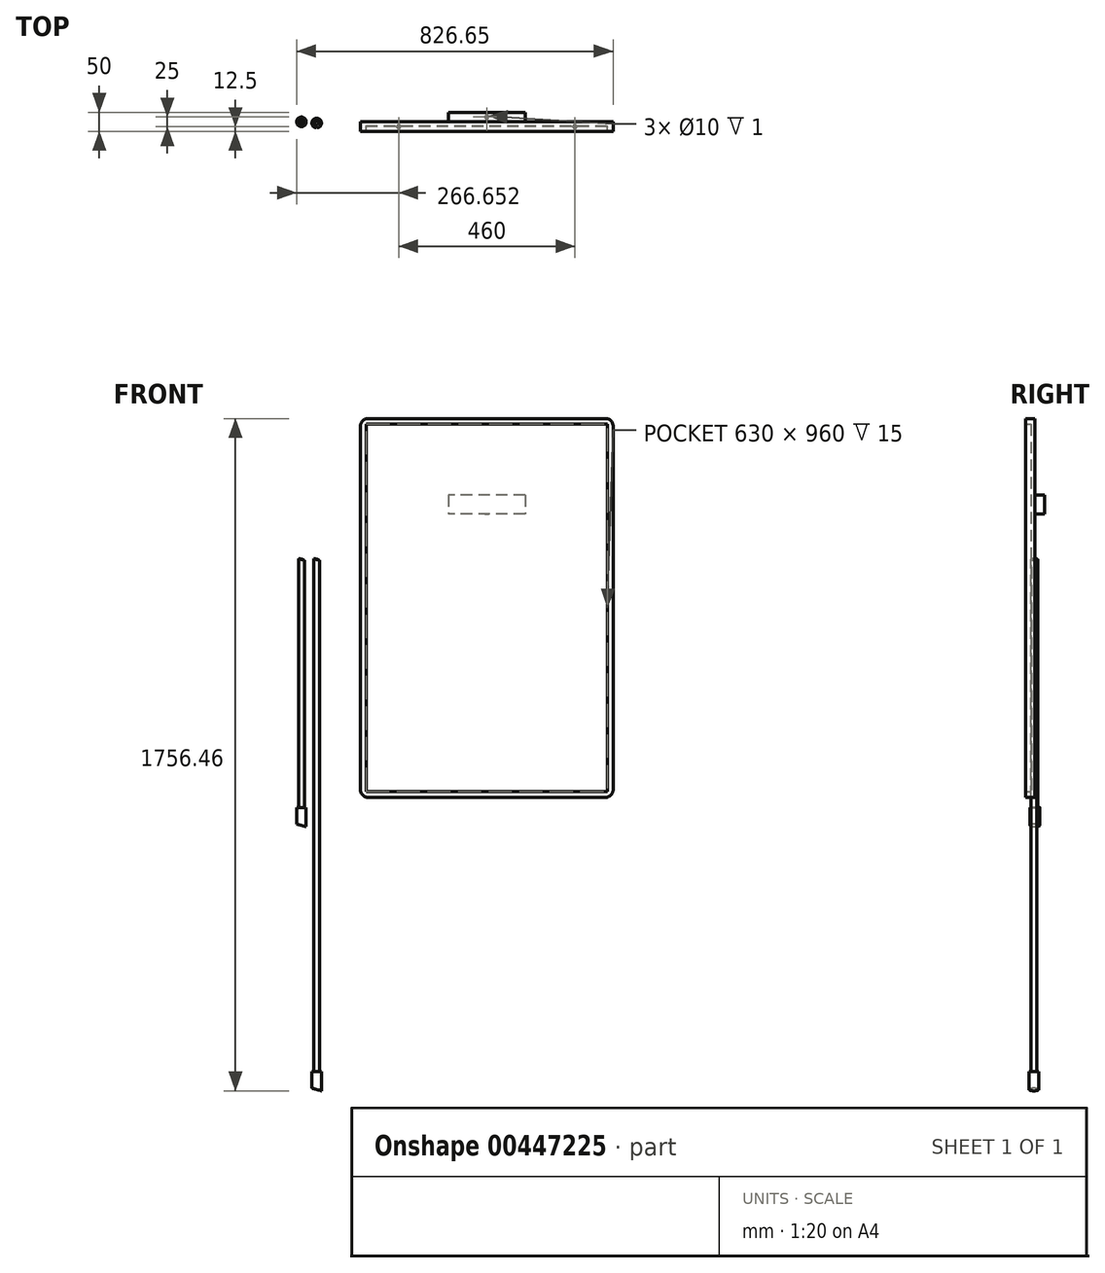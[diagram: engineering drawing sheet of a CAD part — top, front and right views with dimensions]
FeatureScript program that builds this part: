
annotation { "Feature Type Name" : "Feature", "Feature Type Description" : "" }
export const myFeature = defineFeature(function(context is Context, id is Id, definition is map)
    precondition{}
    {
        {
            var Q0;
            Q0=qCreatedBy(makeId("Top.planeOp"),FACE);
            var sketch = newSketch(context, id + "F0", { "sketchPlane" : qUnion([Q0])});
            skCircle(sketch, "E0", {"center": v(0, 0) * mm, "radius": 7.5 * mm});
            skCircle(sketch, "E1", {"center": v(39.86, -2.97) * mm, "radius": 7.5 * mm});
            skSolve(sketch);
        }
        {
            var Q0;
            Q0=makeQuery(id+"F0.imprint","IMPRINT",FACE,{"disambiguationData":[TD([[makeQuery(id+"F0.imprint","IMPRINT",EDGE,{"derivedFrom":sQuery(id+"F0.wireOp",EDGE,"E0")}),1.0]])]});
            extrude(context, id + "F1", {"entities" : qUnion([Q0]), "oppositeDirection" : true, "depth" : 700 * mm});
        }
        {
            var Q0;
            Q0=makeQuery(id+"F0.imprint","IMPRINT",FACE,{"disambiguationData":[TD([[makeQuery(id+"F0.imprint","IMPRINT",EDGE,{"derivedFrom":sQuery(id+"F0.wireOp",EDGE,"E1")}),1.0]])]});
            extrude(context, id + "F2", {"entities" : qUnion([Q0]), "oppositeDirection" : true, "depth" : 1390 * mm});
        }
        {
            var Q0;
            Q0=makeQuery(id+"F2.opExtrude","CAP_FACE",FACE,{"disambiguationData":[OSD([sQuery(id+"F0.wireOp",EDGE,"E1")])],"isStart":false});
            var sketch = newSketch(context, id + "F3", { "sketchPlane" : qUnion([Q0])});
            skCircle(sketch, "E2", {"center": v(39.86, 2.97) * mm, "radius": 12.5 * mm});
            skSolve(sketch);
        }
        {
            var Q0;
            Q0=makeQuery(id+"F3.imprint","IMPRINT",FACE,{"disambiguationData":[TD([[makeQuery(id+"F3.imprint","IMPRINT",EDGE,{"derivedFrom":sQuery(id+"F3.wireOp",EDGE,"E2")}),1.0]])]});
            extrude(context, id + "F4", {"entities" : qUnion([Q0]), "operationType" : NewBodyOperationType.ADD, "oppositeDirection" : true, "depth" : 50 * mm});
        }
        {
            var Q0;
            Q0=makeQuery(id+"F1.opExtrude","CAP_FACE",FACE,{"disambiguationData":[OSD([sQuery(id+"F0.wireOp",EDGE,"E0")])],"isStart":false});
            var sketch = newSketch(context, id + "F5", { "sketchPlane" : qUnion([Q0])});
            skCircle(sketch, "E3", {"center": v(0, 0) * mm, "radius": 12.5 * mm});
            skSolve(sketch);
        }
        {
            var Q0;
            Q0=makeQuery(id+"F5.imprint","IMPRINT",FACE,{"disambiguationData":[TD([[makeQuery(id+"F5.imprint","IMPRINT",EDGE,{"derivedFrom":sQuery(id+"F5.wireOp",EDGE,"E3")}),1.0]])]});
            extrude(context, id + "F6", {"entities" : qUnion([Q0]), "operationType" : NewBodyOperationType.ADD, "oppositeDirection" : true, "depth" : 50 * mm});
        }
        {
            var Q0;
            Q0=qCreatedBy(makeId("Front.planeOp"),FACE);
            var sketch = newSketch(context, id + "F7", { "sketchPlane" : qUnion([Q0])});
            skLineSegment(sketch, "E4", {"start": v(7.5, 0) * mm, "end": v(-7.5, 0) * mm});
            skLineSegment(sketch, "E5", {"start": v(-7.5, 0) * mm, "end": v(7.5, -4.02) * mm});
            skLineSegment(sketch, "E6", {"start": v(7.5, -4.02) * mm, "end": v(7.5, 0) * mm});
            skLineSegment(sketch, "E7", {"start": v(47.36, 0) * mm, "end": v(32.36, 0) * mm});
            skLineSegment(sketch, "E8", {"start": v(32.36, 0) * mm, "end": v(47.36, -4.02) * mm});
            skLineSegment(sketch, "E9", {"start": v(47.36, -4.02) * mm, "end": v(47.36, 0) * mm});
            skLineSegment(sketch, "E10", {"start": v(12.5, -700) * mm, "end": v(-12.5, -700) * mm});
            skLineSegment(sketch, "E11", {"start": v(52.36, -1390) * mm, "end": v(27.36, -1390) * mm});
            skPoint(sketch, "E12", {"position": v(0, -700) * mm});
            skPoint(sketch, "E13", {"position": v(39.86, -1390) * mm});
            skLineSegment(sketch, "E14", {"start": v(12.5, -700) * mm, "end": v(-12.5, -693.3) * mm});
            skLineSegment(sketch, "E15", {"start": v(-12.5, -693.3) * mm, "end": v(-12.5, -700) * mm});
            skLineSegment(sketch, "E16", {"start": v(52.36, -1390) * mm, "end": v(27.36, -1383.3) * mm});
            skLineSegment(sketch, "E17", {"start": v(27.36, -1383.3) * mm, "end": v(27.36, -1390) * mm});
            skSolve(sketch);
        }
        {
            var Q0;
            Q0 = qSketchRegion(id + "F7", true);
            extrude(context, id + "F8", {"entities" : qUnion([Q0]), "operationType" : NewBodyOperationType.REMOVE, "endBound" : BoundingType.THROUGH_ALL, "oppositeDirection" : true, "depth" : 25 * mm, "hasSecondDirection" : true, "secondDirectionBound" : SecondDirectionBoundingType.THROUGH_ALL, "secondDirectionOppositeDirection" : false, "secondDirectionDepth" : 25 * mm});
        }
        {
            var Q0;
            Q0=qCreatedBy(makeId("Front.planeOp"),FACE);
            var sketch = newSketch(context, id + "F9", { "sketchPlane" : qUnion([Q0])});
            skLineSegment(sketch, "E18.bottom", {"start": v(169.15, 351.46) * mm, "end": v(799.15, 351.46) * mm});
            skLineSegment(sketch, "E18.top", {"start": v(169.15, -608.54) * mm, "end": v(799.15, -608.54) * mm});
            skLineSegment(sketch, "E18.left", {"start": v(169.15, 351.46) * mm, "end": v(169.15, -608.54) * mm});
            skLineSegment(sketch, "E18.right", {"start": v(799.15, 351.46) * mm, "end": v(799.15, -608.54) * mm});
            skSolve(sketch);
        }
        {
            var Q0;
            Q0=makeQuery(id+"F9.imprint","IMPRINT",FACE,{"disambiguationData":[TD([[makeQuery(id+"F9.imprint","IMPRINT",EDGE,{"derivedFrom":sQuery(id+"F9.wireOp",EDGE,"E18.bottom")}),-1.0]])]});
            extrude(context, id + "F10", {"entities" : qUnion([Q0]), "depth" : 10 * mm});
        }
        {
            var Q0;
            Q0=qCreatedBy(makeId("Front.planeOp"),FACE);
            var sketch = newSketch(context, id + "F11", { "sketchPlane" : qUnion([Q0])});
            skLineSegment(sketch, "E19.bottom", {"start": v(169.15, 351.46) * mm, "end": v(799.15, 351.46) * mm});
            skLineSegment(sketch, "E19.top", {"start": v(169.15, -608.54) * mm, "end": v(799.15, -608.54) * mm});
            skLineSegment(sketch, "E19.left", {"start": v(169.15, 351.46) * mm, "end": v(169.15, -608.54) * mm});
            skLineSegment(sketch, "E19.right", {"start": v(799.15, 351.46) * mm, "end": v(799.15, -608.54) * mm});
            skLineSegment(sketch, "E20.0", {"start": v(814.15, 346.46) * mm, "end": v(814.15, -603.54) * mm});
            skLineSegment(sketch, "E20.1", {"start": v(174.15, 366.46) * mm, "end": v(794.15, 366.46) * mm});
            skLineSegment(sketch, "E20.2", {"start": v(154.15, 346.46) * mm, "end": v(154.15, -603.54) * mm});
            skLineSegment(sketch, "E20.3", {"start": v(174.15, -623.54) * mm, "end": v(794.15, -623.54) * mm});
            skPoint(sketch, "E21.visualSharp", {"position": v(154.15, 366.46) * mm});
            skArc(sketch, "E21.filletArc", {"start": v(174.15, 366.46) * mm, "mid": v(160, 360.6) * mm, "end": v(154.15, 346.46) * mm});
            skPoint(sketch, "E22.visualSharp", {"position": v(814.15, 366.46) * mm});
            skArc(sketch, "E22.filletArc", {"start": v(814.15, 346.46) * mm, "mid": v(808.3, 360.6) * mm, "end": v(794.15, 366.46) * mm});
            skPoint(sketch, "E23.visualSharp", {"position": v(814.15, -623.54) * mm});
            skArc(sketch, "E23.filletArc", {"start": v(794.15, -623.54) * mm, "mid": v(808.3, -617.69) * mm, "end": v(814.15, -603.54) * mm});
            skPoint(sketch, "E24.visualSharp", {"position": v(154.15, -623.54) * mm});
            skArc(sketch, "E24.filletArc", {"start": v(154.15, -603.54) * mm, "mid": v(160, -617.69) * mm, "end": v(174.15, -623.54) * mm});
            skSolve(sketch);
        }
        {
            var Q0;
            Q0 = qSketchRegion(id + "F11", true);
            extrude(context, id + "F12", {"entities" : qUnion([Q0]), "operationType" : NewBodyOperationType.ADD, "depth" : 25 * mm});
        }
        {
            var Q0;
            Q0=makeQuery(id+"F12.opExtrude","SWEPT_FACE",FACE,{"disambiguationData":[OSD([sQuery(id+"F11.wireOp",EDGE,"E20.3")])]});
            var sketch = newSketch(context, id + "F13", { "sketchPlane" : qUnion([Q0])});
            skCircle(sketch, "E25", {"center": v(254.15, 12.5) * mm, "radius": 5 * mm});
            skLineSegment(sketch, "E26", {"start": v(174.15, 12.5) * mm, "end": v(794.15, 12.5) * mm, "construction": true});
            skCircle(sketch, "E27", {"center": v(714.15, 12.5) * mm, "radius": 5 * mm});
            skSolve(sketch);
        }
        {
            var Q0;
            Q0 = qSketchRegion(id + "F13", true);
            extrude(context, id + "F14", {"entities" : qUnion([Q0]), "operationType" : NewBodyOperationType.REMOVE, "oppositeDirection" : true, "depth" : mm});
        }
        {
            var Q0;
            Q0=makeQuery(id+"F8.boolean.opBoolean","COPY",FACE,{"derivedFrom":makeQuery(id+"F8.opExtrude","SWEPT_FACE",FACE,{"disambiguationData":[OSD([sQuery(id+"F7.wireOp",EDGE,"E5")])]})});
            var sketch = newSketch(context, id + "F15", { "sketchPlane" : qUnion([Q0])});
            skCircle(sketch, "E28", {"center": v(0, 0) * mm, "radius": 5 * mm});
            skSolve(sketch);
        }
        {
            var Q0;
            Q0 = qSketchRegion(id + "F15", true);
            extrude(context, id + "F16", {"entities" : qUnion([Q0]), "operationType" : NewBodyOperationType.ADD, "depth" : 1 * mm});
        }
        {
            var Q0;
            Q0=makeQuery(id+"F8.boolean.opBoolean","COPY",FACE,{"derivedFrom":makeQuery(id+"F8.opExtrude","SWEPT_FACE",FACE,{"disambiguationData":[OSD([sQuery(id+"F7.wireOp",EDGE,"E8")])]})});
            var sketch = newSketch(context, id + "F17", { "sketchPlane" : qUnion([Q0])});
            skCircle(sketch, "E29", {"center": v(38.5, -2.97) * mm, "radius": 5 * mm});
            skSolve(sketch);
        }
        {
            var Q0;
            Q0 = qSketchRegion(id + "F17", true);
            extrude(context, id + "F18", {"entities" : qUnion([Q0]), "operationType" : NewBodyOperationType.ADD, "depth" : 1 * mm});
        }
        {
            var Q0;
            Q0=makeQuery(id+"F12.boolean.opBoolean","MERGE",FACE,{"derivedFrom":[makeQuery(id+"F10.opExtrude","CAP_FACE",FACE,{"disambiguationData":[OSD([sQuery(id+"F9.wireOp",EDGE,"E18.bottom"),sQuery(id+"F9.wireOp",EDGE,"E18.top"),sQuery(id+"F9.wireOp",EDGE,"E18.left"),sQuery(id+"F9.wireOp",EDGE,"E18.right")])],"isStart":true}),makeQuery(id+"F12.opExtrude","CAP_FACE",FACE,{"disambiguationData":[OSD([sQuery(id+"F11.wireOp",EDGE,"E19.bottom"),sQuery(id+"F11.wireOp",EDGE,"E19.top"),sQuery(id+"F11.wireOp",EDGE,"E19.left"),sQuery(id+"F11.wireOp",EDGE,"E19.right"),sQuery(id+"F11.wireOp",EDGE,"E20.0"),sQuery(id+"F11.wireOp",EDGE,"E20.1"),sQuery(id+"F11.wireOp",EDGE,"E20.2"),sQuery(id+"F11.wireOp",EDGE,"E20.3"),sQuery(id+"F11.wireOp",EDGE,"E21.filletArc"),sQuery(id+"F11.wireOp",EDGE,"E22.filletArc"),sQuery(id+"F11.wireOp",EDGE,"E23.filletArc"),sQuery(id+"F11.wireOp",EDGE,"E24.filletArc")])],"isStart":true})]});
            var sketch = newSketch(context, id + "F19", { "sketchPlane" : qUnion([Q0])});
            skLineSegment(sketch, "E30.bottom", {"start": v(-584.15, 166.46) * mm, "end": v(-384.15, 166.46) * mm});
            skLineSegment(sketch, "E30.top", {"start": v(-584.15, 116.46) * mm, "end": v(-384.15, 116.46) * mm});
            skLineSegment(sketch, "E30.left", {"start": v(-584.15, 166.46) * mm, "end": v(-584.15, 116.46) * mm});
            skLineSegment(sketch, "E30.right", {"start": v(-384.15, 166.46) * mm, "end": v(-384.15, 116.46) * mm});
            skLineSegment(sketch, "E31", {"start": v(-814.15, 172.69) * mm, "end": v(-154.15, 172.69) * mm, "construction": true});
            skPoint(sketch, "E32", {"position": v(-484.15, 166.46) * mm});
            skPoint(sketch, "E33", {"position": v(-484.15, 172.69) * mm});
            skSolve(sketch);
        }
        {
            var Q0;
            Q0 = qSketchRegion(id + "F19", true);
            extrude(context, id + "F20", {"entities" : qUnion([Q0]), "operationType" : NewBodyOperationType.ADD, "depth" : 25 * mm});
        }
        {
            var Q0;
            Q0=makeQuery(id+"F20.opExtrude","SWEPT_FACE",FACE,{"disambiguationData":[OSD([sQuery(id+"F19.wireOp",EDGE,"E30.top")])]});
            var sketch = newSketch(context, id + "F21", { "sketchPlane" : qUnion([Q0])});
            skCircle(sketch, "E34", {"center": v(484.15, -12.5) * mm, "radius": 5 * mm});
            skLineSegment(sketch, "E35", {"start": v(484.15, -25) * mm, "end": v(484.15, 0) * mm, "construction": true});
            skSolve(sketch);
        }
        {
            var Q0;
            Q0 = qSketchRegion(id + "F21", true);
            extrude(context, id + "F22", {"entities" : qUnion([Q0]), "operationType" : NewBodyOperationType.REMOVE, "oppositeDirection" : true, "depth" : 1 * mm});
        }
        {
            var Q0;
            Q0=makeQuery(id+"F10.opExtrude","CAP_FACE",FACE,{"disambiguationData":[OSD([sQuery(id+"F9.wireOp",EDGE,"E18.bottom"),sQuery(id+"F9.wireOp",EDGE,"E18.top"),sQuery(id+"F9.wireOp",EDGE,"E18.left"),sQuery(id+"F9.wireOp",EDGE,"E18.right")])],"isStart":false});
            var sketch = newSketch(context, id + "F23", { "sketchPlane" : qUnion([Q0])});
            skLineSegment(sketch, "E36.bottom", {"start": v(169.15, 351.46) * mm, "end": v(799.15, 351.46) * mm});
            skLineSegment(sketch, "E36.top", {"start": v(169.15, -608.54) * mm, "end": v(799.15, -608.54) * mm});
            skLineSegment(sketch, "E36.left", {"start": v(169.15, 351.46) * mm, "end": v(169.15, -608.54) * mm});
            skLineSegment(sketch, "E36.right", {"start": v(799.15, 351.46) * mm, "end": v(799.15, -608.54) * mm});
            skSolve(sketch);
        }
        {
            var Q0;
            Q0 = qSketchRegion(id + "F23", true);
            extrude(context, id + "F24", {"entities" : qUnion([Q0]), "depth" : 1 * mm});
        }
        {
            var Q0;
            Q0=qCreatedBy(makeId("Right.planeOp"),FACE);
            var sketch = newSketch(context, id + "F25", { "sketchPlane" : qUnion([Q0])});
            skFitSpline(sketch, "E37", {"points": [v(-51.5, -592.77) * mm, v(-24.46, -96.86) * mm, v(-36.26, 336.8) * mm, v(-22.87, 370.58) * mm, v(1.7, 372) * mm, v(17.92, 339.54) * mm, v(1.7, 328.72) * mm], "startDerivative": vector(115.67, 1318.86) * mm, "endDerivative": vector(-312.65, -89.42) * mm});
            skFitSpline(sketch, "E38.0", {"points": [v(-50.51, -592.86) * mm, v(-48.1, -565.39) * mm, v(-43.15, -509.91) * mm, v(-37.19, -438.78) * mm, v(-32.9, -380.49) * mm, v(-30, -336) * mm, v(-27.5, -290.68) * mm, v(-25.5, -244.45) * mm, v(-24.08, -197.22) * mm, v(-23.32, -148.94) * mm, v(-23.3, -107.75) * mm, v(-23.7, -74.19) * mm, v(-24.36, -40.34) * mm, v(-25.57, 2.24) * mm, v(-27.47, 52.98) * mm, v(-29.6, 102.54) * mm, v(-31.77, 150.13) * mm, v(-33.77, 194.93) * mm, v(-35.4, 236.13) * mm, v(-36.28, 266.8) * mm, v(-36.59, 288.71) * mm, v(-36.6, 303.75) * mm, v(-36.38, 317.27) * mm, v(-35.96, 327.2) * mm, v(-35.48, 334.28) * mm, v(-35.05, 339.14) * mm, v(-34.53, 343.57) * mm, v(-33.72, 348.91) * mm, v(-32.47, 354.62) * mm, v(-30.52, 360.1) * mm, v(-28.47, 363.69) * mm, v(-26.56, 366.1) * mm, v(-24.97, 367.72) * mm, v(-23.2, 369.16) * mm, v(-21.26, 370.47) * mm, v(-19.14, 371.63) * mm, v(-16.14, 372.92) * mm, v(-12.12, 373.99) * mm, v(-7.9, 374.14) * mm, v(-4.54, 373.59) * mm, v(-2.02, 372.82) * mm, v(0.04, 371.84) * mm, v(1.66, 370.85) * mm, v(3.27, 369.7) * mm, v(5.24, 368.02) * mm, v(8.23, 364.86) * mm, v(11.62, 360.22) * mm, v(14.27, 355.1) * mm, v(15.84, 351.02) * mm, v(16.7, 348.02) * mm, v(17.21, 345.17) * mm, v(17.37, 342.55) * mm, v(17.13, 340.23) * mm, v(16.5, 338.29) * mm, v(15.52, 336.63) * mm, v(14.2, 335.2) * mm, v(12.56, 333.96) * mm, v(10.02, 332.53) * mm, v(6.3, 331.09) * mm, v(3.04, 330.15) * mm, v(1.42, 329.68) * mm]});
            skLineSegment(sketch, "E39", {"start": v(1.42, 329.68) * mm, "end": v(1.7, 328.72) * mm});
            skLineSegment(sketch, "E40", {"start": v(-51.5, -592.77) * mm, "end": v(-50.51, -592.86) * mm});
            skSolve(sketch);
        }
        {
            var Q0;
            Q0=sQuery(id+"F25.wireOp",EDGE,"E37");
            var Q1;
            Q1=sQuery(id+"F25.wireOp",EDGE,"E38.0");
            var Q2;
            Q2=sQuery(id+"F25.wireOp",EDGE,"E40");
            var Q3;
            Q3=sQuery(id+"F25.wireOp",EDGE,"E39");
            extrude(context, id + "F26", {"bodyType" : ToolBodyType.SURFACE, "surfaceEntities" : qUnion([Q0, Q1, Q2, Q3]), "depth" : 630 * mm});
        }
    });
